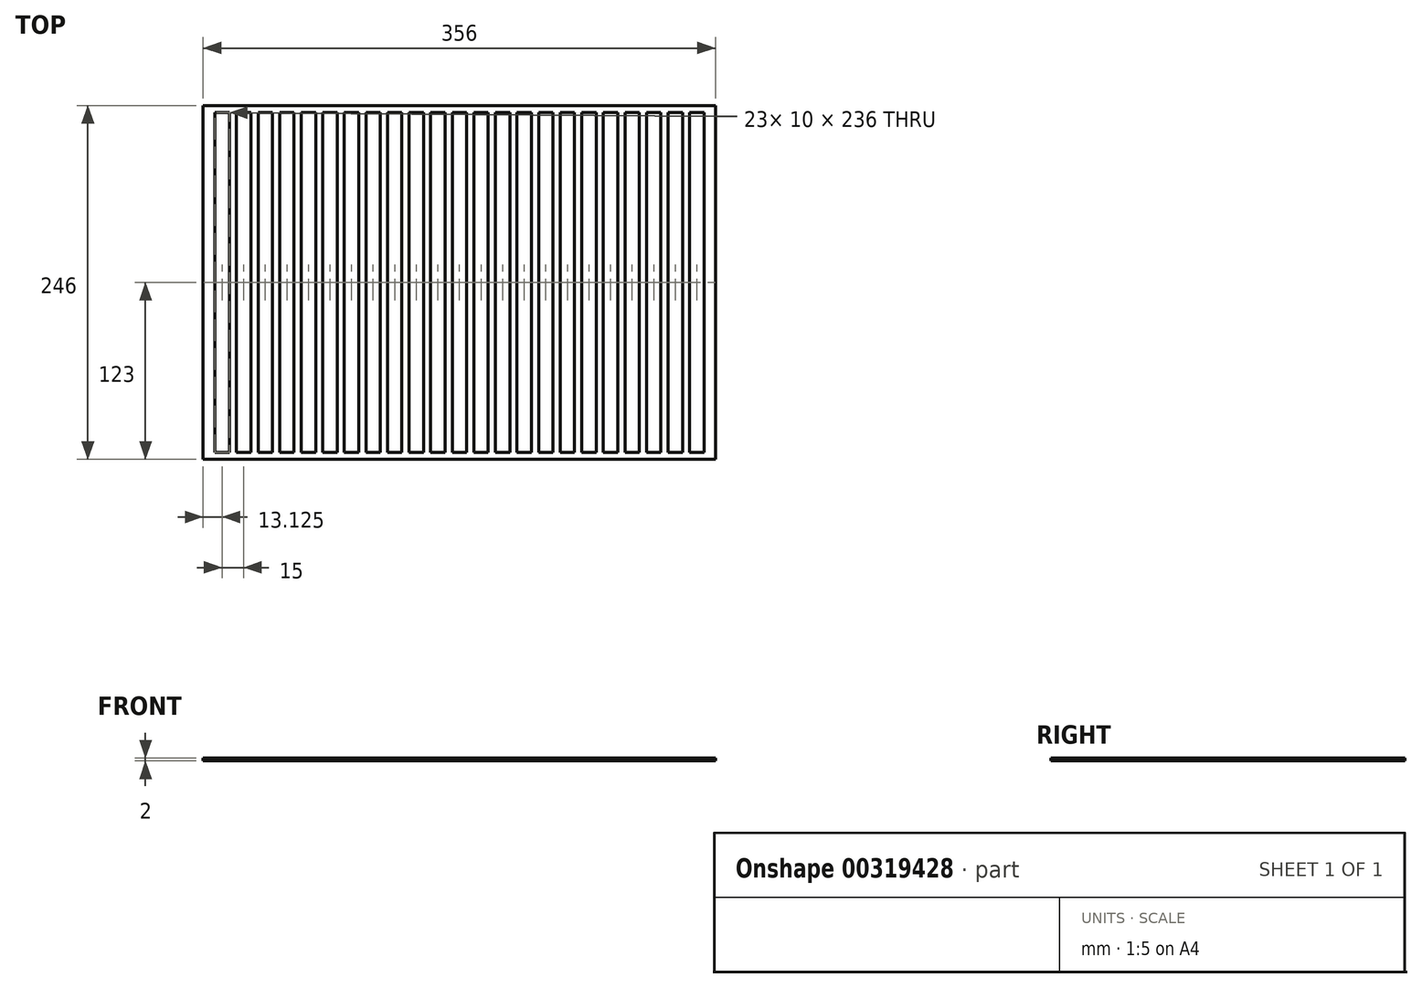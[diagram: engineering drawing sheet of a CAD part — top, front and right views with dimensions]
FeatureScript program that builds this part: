
annotation { "Feature Type Name" : "Feature", "Feature Type Description" : "" }
export const myFeature = defineFeature(function(context is Context, id is Id, definition is map)
    precondition{}
    {
        {
            var Q0;
            Q0=qCreatedBy(makeId("Top.planeOp"),FACE);
            var sketch = newSketch(context, id + "F0", { "sketchPlane" : qUnion([Q0])});
            skLineSegment(sketch, "E0.bottom", {"start": v(-178, 123) * mm, "end": v(178, 123) * mm});
            skLineSegment(sketch, "E0.top", {"start": v(-178, -123) * mm, "end": v(178, -123) * mm});
            skLineSegment(sketch, "E0.left", {"start": v(-178, 123) * mm, "end": v(-178, -123) * mm});
            skLineSegment(sketch, "E0.right", {"start": v(178, 123) * mm, "end": v(178, -123) * mm});
            skLineSegment(sketch, "E1", {"start": v(0, 123) * mm, "end": v(0, -123) * mm, "construction": true});
            skLineSegment(sketch, "E2", {"start": v(-178, 0) * mm, "end": v(178, 0) * mm, "construction": true});
            skSolve(sketch);
        }
        {
            var Q0;
            Q0=makeQuery(id+"F0.imprint","IMPRINT",FACE,{"disambiguationData":[TD([[makeQuery(id+"F0.imprint","IMPRINT",EDGE,{"derivedFrom":sQuery(id+"F0.wireOp",EDGE,"E0.bottom")}),-1.0]])]});
            extrude(context, id + "F1", {"entities" : qUnion([Q0]), "depth" : 2 * mm});
        }
        {
            var Q0;
            Q0=qCreatedBy(makeId("Top.planeOp"),FACE);
            var sketch = newSketch(context, id + "F2", { "sketchPlane" : qUnion([Q0])});
            skLineSegment(sketch, "E3.bottom", {"start": v(-169.87, 118) * mm, "end": v(-159.87, 118) * mm});
            skLineSegment(sketch, "E3.top", {"start": v(-169.87, -118) * mm, "end": v(-159.87, -118) * mm});
            skLineSegment(sketch, "E3.left", {"start": v(-169.87, 118) * mm, "end": v(-169.87, -118) * mm});
            skLineSegment(sketch, "E3.right", {"start": v(-159.87, 118) * mm, "end": v(-159.87, -118) * mm});
            skLineSegment(sketch, "E4.1.0.0", {"start": v(-144.87, 118) * mm, "end": v(-144.87, -118) * mm});
            skLineSegment(sketch, "E4.1.0.1", {"start": v(-154.87, -118) * mm, "end": v(-144.87, -118) * mm});
            skLineSegment(sketch, "E4.1.0.2", {"start": v(-154.87, 118) * mm, "end": v(-144.87, 118) * mm});
            skLineSegment(sketch, "E4.1.0.3", {"start": v(-154.87, 118) * mm, "end": v(-154.87, -118) * mm});
            skLineSegment(sketch, "E4.2.0.0", {"start": v(-129.87, 118) * mm, "end": v(-129.87, -118) * mm});
            skLineSegment(sketch, "E4.2.0.1", {"start": v(-139.87, -118) * mm, "end": v(-129.87, -118) * mm});
            skLineSegment(sketch, "E4.2.0.2", {"start": v(-139.87, 118) * mm, "end": v(-129.87, 118) * mm});
            skLineSegment(sketch, "E4.2.0.3", {"start": v(-139.87, 118) * mm, "end": v(-139.87, -118) * mm});
            skLineSegment(sketch, "E4.direction1", {"start": v(-169.87, -118) * mm, "end": v(-154.87, -118) * mm, "construction": true});
            skLineSegment(sketch, "E5.0.3.0", {"start": v(-114.87, 118) * mm, "end": v(-114.87, -118) * mm});
            skLineSegment(sketch, "E5.3.3.0", {"start": v(-124.87, -118) * mm, "end": v(-114.87, -118) * mm});
            skLineSegment(sketch, "E5.6.3.0", {"start": v(-124.87, 118) * mm, "end": v(-114.87, 118) * mm});
            skLineSegment(sketch, "E5.9.3.0", {"start": v(-124.87, 118) * mm, "end": v(-124.87, -118) * mm});
            skLineSegment(sketch, "E5.0.4.0", {"start": v(-99.87, 118) * mm, "end": v(-99.87, -118) * mm});
            skLineSegment(sketch, "E5.3.4.0", {"start": v(-109.87, -118) * mm, "end": v(-99.87, -118) * mm});
            skLineSegment(sketch, "E5.6.4.0", {"start": v(-109.87, 118) * mm, "end": v(-99.87, 118) * mm});
            skLineSegment(sketch, "E5.9.4.0", {"start": v(-109.87, 118) * mm, "end": v(-109.87, -118) * mm});
            skLineSegment(sketch, "E5.0.5.0", {"start": v(-84.87, 118) * mm, "end": v(-84.87, -118) * mm});
            skLineSegment(sketch, "E5.3.5.0", {"start": v(-94.87, -118) * mm, "end": v(-84.87, -118) * mm});
            skLineSegment(sketch, "E5.6.5.0", {"start": v(-94.87, 118) * mm, "end": v(-84.87, 118) * mm});
            skLineSegment(sketch, "E5.9.5.0", {"start": v(-94.87, 118) * mm, "end": v(-94.87, -118) * mm});
            skLineSegment(sketch, "E5.0.6.0", {"start": v(-69.87, 118) * mm, "end": v(-69.87, -118) * mm});
            skLineSegment(sketch, "E5.3.6.0", {"start": v(-79.87, -118) * mm, "end": v(-69.87, -118) * mm});
            skLineSegment(sketch, "E5.6.6.0", {"start": v(-79.87, 118) * mm, "end": v(-69.87, 118) * mm});
            skLineSegment(sketch, "E5.9.6.0", {"start": v(-79.87, 118) * mm, "end": v(-79.87, -118) * mm});
            skLineSegment(sketch, "E5.0.7.0", {"start": v(-54.87, 118) * mm, "end": v(-54.87, -118) * mm});
            skLineSegment(sketch, "E5.3.7.0", {"start": v(-64.87, -118) * mm, "end": v(-54.87, -118) * mm});
            skLineSegment(sketch, "E5.6.7.0", {"start": v(-64.87, 118) * mm, "end": v(-54.87, 118) * mm});
            skLineSegment(sketch, "E5.9.7.0", {"start": v(-64.87, 118) * mm, "end": v(-64.87, -118) * mm});
            skLineSegment(sketch, "E5.0.8.0", {"start": v(-39.87, 118) * mm, "end": v(-39.87, -118) * mm});
            skLineSegment(sketch, "E5.3.8.0", {"start": v(-49.87, -118) * mm, "end": v(-39.87, -118) * mm});
            skLineSegment(sketch, "E5.6.8.0", {"start": v(-49.87, 118) * mm, "end": v(-39.87, 118) * mm});
            skLineSegment(sketch, "E5.9.8.0", {"start": v(-49.87, 118) * mm, "end": v(-49.87, -118) * mm});
            skLineSegment(sketch, "E5.0.9.0", {"start": v(-24.87, 118) * mm, "end": v(-24.87, -118) * mm});
            skLineSegment(sketch, "E5.3.9.0", {"start": v(-34.87, -118) * mm, "end": v(-24.87, -118) * mm});
            skLineSegment(sketch, "E5.6.9.0", {"start": v(-34.87, 118) * mm, "end": v(-24.87, 118) * mm});
            skLineSegment(sketch, "E5.9.9.0", {"start": v(-34.87, 118) * mm, "end": v(-34.87, -118) * mm});
            skLineSegment(sketch, "E5.0.10.0", {"start": v(-9.87, 118) * mm, "end": v(-9.87, -118) * mm});
            skLineSegment(sketch, "E5.3.10.0", {"start": v(-19.87, -118) * mm, "end": v(-9.87, -118) * mm});
            skLineSegment(sketch, "E5.6.10.0", {"start": v(-19.87, 118) * mm, "end": v(-9.87, 118) * mm});
            skLineSegment(sketch, "E5.9.10.0", {"start": v(-19.87, 118) * mm, "end": v(-19.87, -118) * mm});
            skLineSegment(sketch, "E5.0.11.0", {"start": v(5.13, 118) * mm, "end": v(5.13, -118) * mm});
            skLineSegment(sketch, "E5.3.11.0", {"start": v(-4.87, -118) * mm, "end": v(5.13, -118) * mm});
            skLineSegment(sketch, "E5.6.11.0", {"start": v(-4.87, 118) * mm, "end": v(5.13, 118) * mm});
            skLineSegment(sketch, "E5.9.11.0", {"start": v(-4.87, 118) * mm, "end": v(-4.87, -118) * mm});
            skLineSegment(sketch, "E5.0.12.0", {"start": v(20.13, 118) * mm, "end": v(20.13, -118) * mm});
            skLineSegment(sketch, "E5.3.12.0", {"start": v(10.13, -118) * mm, "end": v(20.13, -118) * mm});
            skLineSegment(sketch, "E5.6.12.0", {"start": v(10.13, 118) * mm, "end": v(20.13, 118) * mm});
            skLineSegment(sketch, "E5.9.12.0", {"start": v(10.13, 118) * mm, "end": v(10.13, -118) * mm});
            skLineSegment(sketch, "E5.0.13.0", {"start": v(35.13, 118) * mm, "end": v(35.13, -118) * mm});
            skLineSegment(sketch, "E5.3.13.0", {"start": v(25.13, -118) * mm, "end": v(35.13, -118) * mm});
            skLineSegment(sketch, "E5.6.13.0", {"start": v(25.13, 118) * mm, "end": v(35.13, 118) * mm});
            skLineSegment(sketch, "E5.9.13.0", {"start": v(25.13, 118) * mm, "end": v(25.13, -118) * mm});
            skLineSegment(sketch, "E5.0.14.0", {"start": v(50.13, 118) * mm, "end": v(50.13, -118) * mm});
            skLineSegment(sketch, "E5.3.14.0", {"start": v(40.13, -118) * mm, "end": v(50.13, -118) * mm});
            skLineSegment(sketch, "E5.6.14.0", {"start": v(40.13, 118) * mm, "end": v(50.13, 118) * mm});
            skLineSegment(sketch, "E5.9.14.0", {"start": v(40.13, 118) * mm, "end": v(40.13, -118) * mm});
            skLineSegment(sketch, "E6.0.15.0", {"start": v(65.13, 118) * mm, "end": v(65.13, -118) * mm});
            skLineSegment(sketch, "E6.3.15.0", {"start": v(55.13, -118) * mm, "end": v(65.13, -118) * mm});
            skLineSegment(sketch, "E6.6.15.0", {"start": v(55.13, 118) * mm, "end": v(65.13, 118) * mm});
            skLineSegment(sketch, "E6.9.15.0", {"start": v(55.13, 118) * mm, "end": v(55.13, -118) * mm});
            skLineSegment(sketch, "E6.0.16.0", {"start": v(80.13, 118) * mm, "end": v(80.13, -118) * mm});
            skLineSegment(sketch, "E6.3.16.0", {"start": v(70.13, -118) * mm, "end": v(80.13, -118) * mm});
            skLineSegment(sketch, "E6.6.16.0", {"start": v(70.13, 118) * mm, "end": v(80.13, 118) * mm});
            skLineSegment(sketch, "E6.9.16.0", {"start": v(70.13, 118) * mm, "end": v(70.13, -118) * mm});
            skLineSegment(sketch, "E6.0.17.0", {"start": v(95.13, 118) * mm, "end": v(95.13, -118) * mm});
            skLineSegment(sketch, "E6.3.17.0", {"start": v(85.13, -118) * mm, "end": v(95.13, -118) * mm});
            skLineSegment(sketch, "E6.6.17.0", {"start": v(85.13, 118) * mm, "end": v(95.13, 118) * mm});
            skLineSegment(sketch, "E6.9.17.0", {"start": v(85.13, 118) * mm, "end": v(85.13, -118) * mm});
            skLineSegment(sketch, "E6.0.18.0", {"start": v(110.13, 118) * mm, "end": v(110.13, -118) * mm});
            skLineSegment(sketch, "E6.3.18.0", {"start": v(100.13, -118) * mm, "end": v(110.13, -118) * mm});
            skLineSegment(sketch, "E6.6.18.0", {"start": v(100.13, 118) * mm, "end": v(110.13, 118) * mm});
            skLineSegment(sketch, "E6.9.18.0", {"start": v(100.13, 118) * mm, "end": v(100.13, -118) * mm});
            skLineSegment(sketch, "E6.0.19.0", {"start": v(125.13, 118) * mm, "end": v(125.13, -118) * mm});
            skLineSegment(sketch, "E6.3.19.0", {"start": v(115.13, -118) * mm, "end": v(125.13, -118) * mm});
            skLineSegment(sketch, "E6.6.19.0", {"start": v(115.13, 118) * mm, "end": v(125.13, 118) * mm});
            skLineSegment(sketch, "E6.9.19.0", {"start": v(115.13, 118) * mm, "end": v(115.13, -118) * mm});
            skLineSegment(sketch, "E7.0.20.0", {"start": v(140.13, 118) * mm, "end": v(140.13, -118) * mm});
            skLineSegment(sketch, "E7.3.20.0", {"start": v(130.13, -118) * mm, "end": v(140.13, -118) * mm});
            skLineSegment(sketch, "E7.6.20.0", {"start": v(130.13, 118) * mm, "end": v(140.13, 118) * mm});
            skLineSegment(sketch, "E7.9.20.0", {"start": v(130.13, 118) * mm, "end": v(130.13, -118) * mm});
            skLineSegment(sketch, "E7.0.21.0", {"start": v(155.13, 118) * mm, "end": v(155.13, -118) * mm});
            skLineSegment(sketch, "E7.3.21.0", {"start": v(145.13, -118) * mm, "end": v(155.13, -118) * mm});
            skLineSegment(sketch, "E7.6.21.0", {"start": v(145.13, 118) * mm, "end": v(155.13, 118) * mm});
            skLineSegment(sketch, "E7.9.21.0", {"start": v(145.13, 118) * mm, "end": v(145.13, -118) * mm});
            skLineSegment(sketch, "E8.0.22.0", {"start": v(170.13, 118) * mm, "end": v(170.13, -118) * mm});
            skLineSegment(sketch, "E8.3.22.0", {"start": v(160.13, -118) * mm, "end": v(170.13, -118) * mm});
            skLineSegment(sketch, "E8.6.22.0", {"start": v(160.13, 118) * mm, "end": v(170.13, 118) * mm});
            skLineSegment(sketch, "E8.9.22.0", {"start": v(160.13, 118) * mm, "end": v(160.13, -118) * mm});
            skSolve(sketch);
        }
        {
            var Q0;
            Q0 = qSketchRegion(id + "F2", true);
            extrude(context, id + "F3", {"entities" : qUnion([Q0]), "operationType" : NewBodyOperationType.REMOVE, "depth" : 5 * mm});
        }
    });
